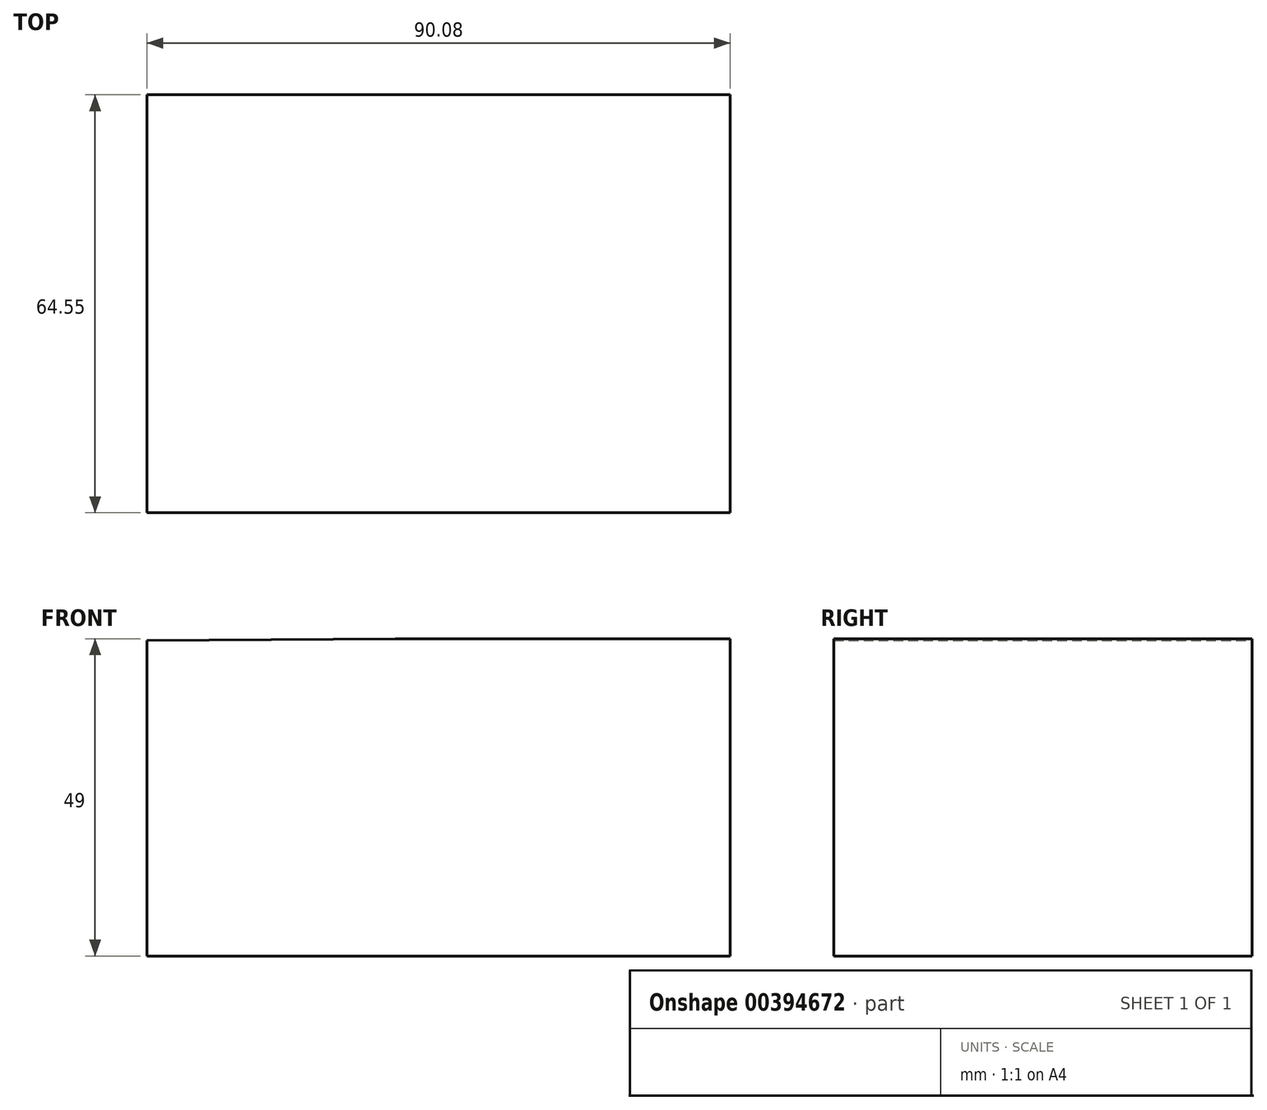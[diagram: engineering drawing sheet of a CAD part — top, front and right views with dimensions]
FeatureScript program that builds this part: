
annotation { "Feature Type Name" : "Feature", "Feature Type Description" : "" }
export const myFeature = defineFeature(function(context is Context, id is Id, definition is map)
    precondition{}
    {
        {
            var Q0;
            Q0=qCreatedBy(makeId("Front.planeOp"),FACE);
            var sketch = newSketch(context, id + "F0", { "sketchPlane" : qUnion([Q0])});
            skLineSegment(sketch, "E0", {"start": v(0, 19.95) * mm, "end": v(51.72, 19.95) * mm});
            skLineSegment(sketch, "E1", {"start": v(51.72, 19.95) * mm, "end": v(51.72, -29.05) * mm});
            skLineSegment(sketch, "E2", {"start": v(51.72, -29.05) * mm, "end": v(-38.36, -29.05) * mm});
            skLineSegment(sketch, "E3", {"start": v(-38.36, -29.05) * mm, "end": v(-38.36, 19.68) * mm});
            skLineSegment(sketch, "E4", {"start": v(-38.36, 19.68) * mm, "end": v(0, 19.95) * mm});
            skSolve(sketch);
        }
        {
            var Q0;
            Q0=makeQuery(id+"F0.imprint","IMPRINT",FACE,{"disambiguationData":[TD([[makeQuery(id+"F0.imprint","IMPRINT",EDGE,{"derivedFrom":sQuery(id+"F0.wireOp",EDGE,"E0")}),-1.0]])]});
            extrude(context, id + "F1", {"entities" : qUnion([Q0]), "depth" : 64.55 * mm});
        }
    });
